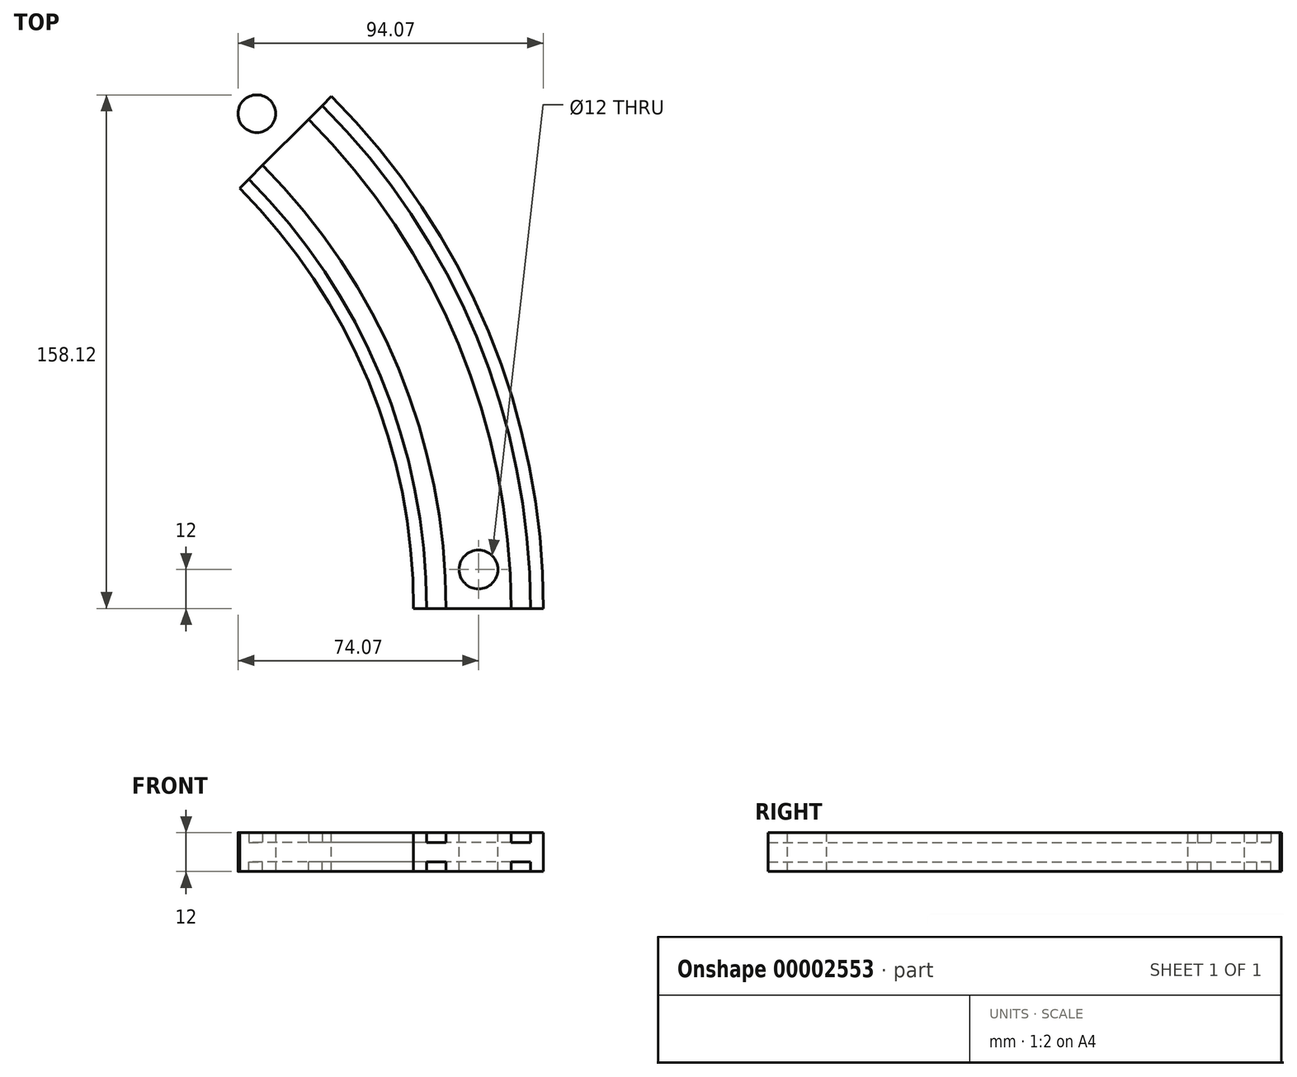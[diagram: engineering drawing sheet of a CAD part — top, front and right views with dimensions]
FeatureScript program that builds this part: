
annotation { "Feature Type Name" : "Feature", "Feature Type Description" : "" }
export const myFeature = defineFeature(function(context is Context, id is Id, definition is map)
    precondition{}
    {
        {
            var Q0;
            Q0=qCreatedBy(makeId("Front.planeOp"),FACE);
            var sketch = newSketch(context, id + "F0", { "sketchPlane" : qUnion([Q0])});
            skLineSegment(sketch, "E0.bottom", {"start": v(0, 0) * mm, "end": v(40, 0) * mm});
            skLineSegment(sketch, "E0.top", {"start": v(0, 12) * mm, "end": v(40, 12) * mm});
            skLineSegment(sketch, "E0.left", {"start": v(0, 0) * mm, "end": v(0, 12) * mm});
            skLineSegment(sketch, "E0.right", {"start": v(40, 0) * mm, "end": v(40, 12) * mm});
            skLineSegment(sketch, "E1.bottom", {"start": v(36, 12) * mm, "end": v(30, 12) * mm});
            skLineSegment(sketch, "E1.top", {"start": v(36, 9) * mm, "end": v(30, 9) * mm});
            skLineSegment(sketch, "E1.left", {"start": v(36, 12) * mm, "end": v(36, 9) * mm});
            skLineSegment(sketch, "E1.right", {"start": v(30, 12) * mm, "end": v(30, 9) * mm});
            skLineSegment(sketch, "E2", {"start": v(20, 12) * mm, "end": v(20, 0) * mm, "construction": true});
            skLineSegment(sketch, "E3.0.MirrorCS", {"start": v(10, 12) * mm, "end": v(10, 9) * mm});
            skLineSegment(sketch, "E4.0.MirrorCS", {"start": v(4, 9) * mm, "end": v(10, 9) * mm});
            skLineSegment(sketch, "E5.0.MirrorCS", {"start": v(4, 12) * mm, "end": v(4, 9) * mm});
            skLineSegment(sketch, "E6", {"start": v(0, 6) * mm, "end": v(40, 6) * mm});
            skLineSegment(sketch, "E7.0.MirrorCS", {"start": v(4, 0) * mm, "end": v(4, 3) * mm});
            skLineSegment(sketch, "E8.0.MirrorCS", {"start": v(4, 3) * mm, "end": v(10, 3) * mm});
            skLineSegment(sketch, "E9.0.MirrorCS", {"start": v(10, 0) * mm, "end": v(10, 3) * mm});
            skLineSegment(sketch, "E10.0.MirrorCS", {"start": v(30, 0) * mm, "end": v(30, 3) * mm});
            skLineSegment(sketch, "E11.0.MirrorCS", {"start": v(36, 3) * mm, "end": v(30, 3) * mm});
            skLineSegment(sketch, "E12.0.MirrorCS", {"start": v(36, 0) * mm, "end": v(36, 3) * mm});
            skSolve(sketch);
        }
        {
            var Q0;
            Q0=qCreatedBy(makeId("Top.planeOp"),FACE);
            var sketch = newSketch(context, id + "F1", { "sketchPlane" : qUnion([Q0])});
            skArc(sketch, "E13", {"start": v(0, 0) * mm, "mid": v(-13.92, 70) * mm, "end": v(-53.58, 129.34) * mm});
            skLineSegment(sketch, "E14", {"start": v(0, 0) * mm, "end": v(-53.58, 129.34) * mm, "construction": true});
            skLineSegment(sketch, "E15", {"start": v(-53.58, 129.34) * mm, "end": v(-25.3, 157.63) * mm, "construction": true});
            skArc(sketch, "E16", {"start": v(40, 0) * mm, "mid": v(23.03, 85.3) * mm, "end": v(-25.3, 157.63) * mm, "construction": true});
            skPoint(sketch, "E17.0", {"position": v(40, 0) * mm});
            skSolve(sketch);
        }
        {
            var Q0;
            {var subQ4=sQuery(id+"F0.wireOp",EDGE,"E6");Q0=makeQuery(id+"F0.imprint","IMPRINT",FACE,{"disambiguationData":[TD([[makeQuery(id+"F0.imprint","IMPRINT",EDGE,{"derivedFrom":subQ4}),-1.0]])]});}
            var Q1;
            Q1=makeQuery(id+"F0.imprint","IMPRINT",FACE,{"disambiguationData":[TD([[makeQuery(id+"F0.imprint","IMPRINT",EDGE,{"derivedFrom":sQuery(id+"F0.wireOp",EDGE,"E1.top")}),1.0]])]});
            var Q2;
            Q2=sQuery(id+"F1.wireOp",EDGE,"E13");
            sweep(context, id + "F2", {"profiles" : qUnion([Q0, Q1]), "path" : qUnion([Q2])});
        }
        {
            var Q0;
            {var subQ0=sQuery(id+"F0.wireOp",EDGE,"E0.bottom");var subQ1=sQuery(id+"F1.wireOp",EDGE,"E13");Q0=makeQuery(id+"F2.opSweep","SWEPT_FACE",FACE,{"disambiguationData":[OSD([subQ0,subQ1]),TDD([makeQuery(id+"F0.imprint","IMPRINT",EDGE,{"disambiguationData":[TD([[makeQuery(id+"F0.imprint","INTERSECT",VERTEX,{"derivedFrom":[subQ0,sQuery(id+"F0.wireOp",EDGE,"E9.0.MirrorCS")]}),-1.0]])],"derivedFrom":subQ0}),subQ1])]});}
            var sketch = newSketch(context, id + "F3", { "sketchPlane" : qUnion([Q0])});
            skLineSegment(sketch, "E18", {"start": v(-39.43, -143.49) * mm, "end": v(-64.71, -168.76) * mm, "construction": true});
            skLineSegment(sketch, "E19.rect.bottom", {"start": v(-41.38, -141.54) * mm, "end": v(-50.22, -150.38) * mm});
            skLineSegment(sketch, "E19.rect.top", {"start": v(-37.49, -145.43) * mm, "end": v(-46.33, -154.27) * mm});
            skLineSegment(sketch, "E19.rect.left", {"start": v(-41.38, -141.54) * mm, "end": v(-37.49, -145.43) * mm});
            skLineSegment(sketch, "E19.rect.right", {"start": v(-50.22, -150.38) * mm, "end": v(-46.33, -154.27) * mm});
            skPoint(sketch, "E19.rect.middle", {"position": v(-43.85, -147.9) * mm});
            skCircle(sketch, "E20", {"center": v(-48.27, -152.32) * mm, "radius": 5.8 * mm});
            skSolve(sketch);
        }
        {
            var Q0;
            {var subQ5=sQuery(id+"F3.wireOp",EDGE,"E19.rect.right");Q0=makeQuery(id+"F3.imprint","IMPRINT",FACE,{"disambiguationData":[TD([[makeQuery(id+"F3.imprint","IMPRINT",EDGE,{"derivedFrom":subQ5}),-1.0]])]});}
            var Q1;
            {var subQ5=sQuery(id+"F3.wireOp",EDGE,"E19.rect.right");Q1=makeQuery(id+"F3.imprint","IMPRINT",FACE,{"disambiguationData":[TD([[makeQuery(id+"F3.imprint","IMPRINT",EDGE,{"derivedFrom":subQ5}),1.0]])]});}
            var Q2;
            {var subQ5=sQuery(id+"F3.wireOp",EDGE,"E19.rect.left");Q2=makeQuery(id+"F3.imprint","IMPRINT",FACE,{"disambiguationData":[TD([[makeQuery(id+"F3.imprint","IMPRINT",EDGE,{"derivedFrom":subQ5}),-1.0]])]});}
            var Q3;
            {var subQ0=sQuery(id+"F0.wireOp",EDGE,"E0.top");var subQ1=sQuery(id+"F1.wireOp",EDGE,"E13");Q3=makeQuery(id+"F2.opSweep","SWEPT_FACE",FACE,{"disambiguationData":[OSD([subQ0,subQ1]),TDD([makeQuery(id+"F0.imprint","IMPRINT",EDGE,{"disambiguationData":[TD([[makeQuery(id+"F0.imprint","INTERSECT",VERTEX,{"derivedFrom":[subQ0,sQuery(id+"F0.wireOp",EDGE,"E3.0.MirrorCS")]}),-1.0]])],"derivedFrom":subQ0}),subQ1])]});}
            extrude(context, id + "F4", {"entities" : qUnion([Q0, Q1, Q2]), "operationType" : NewBodyOperationType.ADD, "endBound" : BoundingType.UP_TO_SURFACE, "oppositeDirection" : true, "endBoundEntityFace" : qUnion([Q3]), "depth" : 25 * mm});
        }
        {
            var Q0;
            {var subQ0=sQuery(id+"F0.wireOp",EDGE,"E0.top");var subQ1=sQuery(id+"F1.wireOp",EDGE,"E13");Q0=makeQuery(id+"F4.boolean.opBoolean","MERGE",FACE,{"derivedFrom":[makeQuery(id+"F2.opSweep","SWEPT_FACE",FACE,{"disambiguationData":[OSD([subQ0,subQ1]),TDD([makeQuery(id+"F0.imprint","IMPRINT",EDGE,{"disambiguationData":[TD([[makeQuery(id+"F0.imprint","INTERSECT",VERTEX,{"derivedFrom":[subQ0,sQuery(id+"F0.wireOp",EDGE,"E3.0.MirrorCS")]}),-1.0]])],"derivedFrom":subQ0}),subQ1])]}),makeQuery(id+"F4.opExtrude","CAP_FACE",FACE,{"disambiguationData":[OSD([sQuery(id+"F3.wireOp",EDGE,"E19.rect.bottom"),sQuery(id+"F3.wireOp",EDGE,"E19.rect.top"),sQuery(id+"F3.wireOp",EDGE,"E19.rect.left"),sQuery(id+"F3.wireOp",EDGE,"E20")])],"isStart":false})]});}
            var sketch = newSketch(context, id + "F5", { "sketchPlane" : qUnion([Q0])});
            skLineSegment(sketch, "E21.rect.bottom", {"start": v(16.5, 12) * mm, "end": v(23.5, 12) * mm});
            skLineSegment(sketch, "E21.rect.left", {"start": v(16.5, 12) * mm, "end": v(16.5, 0) * mm});
            skLineSegment(sketch, "E21.rect.right", {"start": v(23.5, 12) * mm, "end": v(23.5, 0) * mm});
            skPoint(sketch, "E21.rect.middle", {"position": v(20, 0) * mm});
            skCircle(sketch, "E22", {"center": v(20, 12) * mm, "radius": 6 * mm});
            skLineSegment(sketch, "E23", {"start": v(23.5, 0) * mm, "end": v(16.5, 0) * mm});
            skSolve(sketch);
        }
        {
            var Q0;
            {var subQ6=sQuery(id+"F5.wireOp",EDGE,"E21.rect.bottom");var subQ9=makeQuery(id+"F5.imprint","IMPRINT",EDGE,{"derivedFrom":subQ6});var subQ10=sQuery(id+"F5.wireOp",EDGE,"E23");Q0=qUnion([makeQuery(id+"F5.imprint","IMPRINT",FACE,{"disambiguationData":[TD([[subQ9,-1.0]])]}),makeQuery(id+"F5.imprint","IMPRINT",FACE,{"disambiguationData":[TD([[subQ9,1.0]])]}),makeQuery(id+"F5.imprint","IMPRINT",FACE,{"disambiguationData":[TD([[makeQuery(id+"F5.imprint","IMPRINT",EDGE,{"derivedFrom":subQ10}),-1.0]])]})]);}
            extrude(context, id + "F6", {"entities" : qUnion([Q0]), "operationType" : NewBodyOperationType.REMOVE, "endBound" : BoundingType.UP_TO_NEXT, "oppositeDirection" : true, "depth" : 25 * mm});
        }
    });
